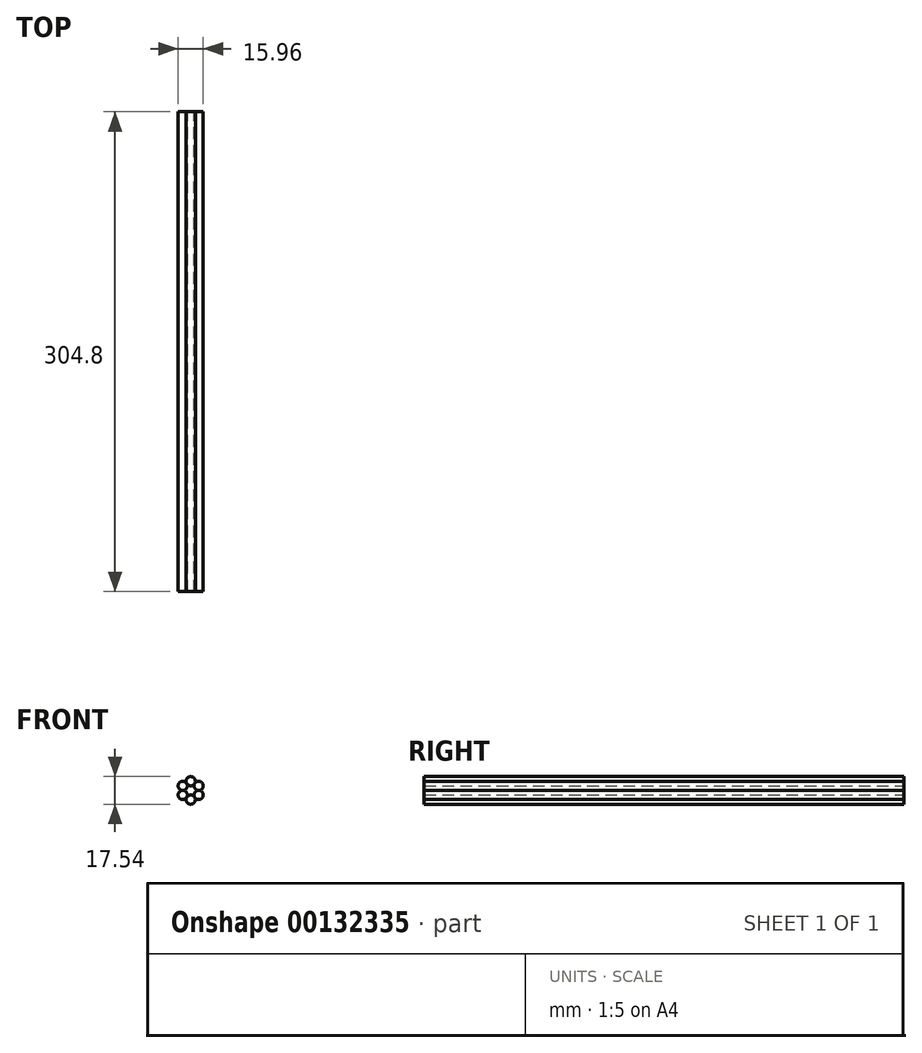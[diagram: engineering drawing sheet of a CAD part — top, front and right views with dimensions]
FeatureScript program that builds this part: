
annotation { "Feature Type Name" : "Feature", "Feature Type Description" : "" }
export const myFeature = defineFeature(function(context is Context, id is Id, definition is map)
    precondition{}
    {
        {
            var Q0;
            Q0=qCreatedBy(makeId("Front.planeOp"),FACE);
            var sketch = newSketch(context, id + "F0", { "sketchPlane" : qUnion([Q0])});
            skCircle(sketch, "E0", {"center": v(0, 0) * mm, "radius": 2.92 * mm});
            skCircle(sketch, "E1", {"center": v(-5.05, -2.93) * mm, "radius": 2.92 * mm});
            skCircle(sketch, "E2", {"center": v(-5.05, -8.77) * mm, "radius": 2.92 * mm});
            skCircle(sketch, "E3", {"center": v(0, -11.7) * mm, "radius": 2.92 * mm});
            skCircle(sketch, "E4", {"center": v(5.05, -8.77) * mm, "radius": 2.92 * mm});
            skCircle(sketch, "E5", {"center": v(5.05, -2.93) * mm, "radius": 2.92 * mm});
            skSolve(sketch);
        }
        {
            var Q0;
            {var subQ0=sQuery(id+"F0.wireOp",EDGE,"E0");var subQ1=makeQuery(id+"F0.imprint","INTERSECT",VERTEX,{"derivedFrom":[subQ0,sQuery(id+"F0.wireOp",EDGE,"E1")]});Q0=makeQuery(id+"F0.imprint","IMPRINT",FACE,{"disambiguationData":[TD([[makeQuery(id+"F0.imprint","IMPRINT",EDGE,{"disambiguationData":[TD([[subQ1,-1.0]])],"derivedFrom":subQ0}),1.0]])]});}
            var Q1;
            {var subQ0=sQuery(id+"F0.wireOp",EDGE,"E1");var subQ1=makeQuery(id+"F0.imprint","INTERSECT",VERTEX,{"derivedFrom":[sQuery(id+"F0.wireOp",EDGE,"E0"),subQ0]});Q1=makeQuery(id+"F0.imprint","IMPRINT",FACE,{"disambiguationData":[TD([[makeQuery(id+"F0.imprint","IMPRINT",EDGE,{"disambiguationData":[TD([[subQ1,-1.0]])],"derivedFrom":subQ0}),1.0]])]});}
            var Q2;
            {var subQ0=sQuery(id+"F0.wireOp",EDGE,"E2");var subQ1=makeQuery(id+"F0.imprint","INTERSECT",VERTEX,{"derivedFrom":[sQuery(id+"F0.wireOp",EDGE,"E1"),subQ0]});Q2=makeQuery(id+"F0.imprint","IMPRINT",FACE,{"disambiguationData":[TD([[makeQuery(id+"F0.imprint","IMPRINT",EDGE,{"disambiguationData":[TD([[subQ1,-1.0]])],"derivedFrom":subQ0}),1.0]])]});}
            var Q3;
            {var subQ0=sQuery(id+"F0.wireOp",EDGE,"E3");var subQ1=makeQuery(id+"F0.imprint","INTERSECT",VERTEX,{"derivedFrom":[sQuery(id+"F0.wireOp",EDGE,"E2"),subQ0]});Q3=makeQuery(id+"F0.imprint","IMPRINT",FACE,{"disambiguationData":[TD([[makeQuery(id+"F0.imprint","IMPRINT",EDGE,{"disambiguationData":[TD([[subQ1,1.0]])],"derivedFrom":subQ0}),1.0]])]});}
            var Q4;
            {var subQ0=sQuery(id+"F0.wireOp",EDGE,"E4");var subQ1=makeQuery(id+"F0.imprint","INTERSECT",VERTEX,{"derivedFrom":[sQuery(id+"F0.wireOp",EDGE,"E3"),subQ0]});Q4=makeQuery(id+"F0.imprint","IMPRINT",FACE,{"disambiguationData":[TD([[makeQuery(id+"F0.imprint","IMPRINT",EDGE,{"disambiguationData":[TD([[subQ1,1.0]])],"derivedFrom":subQ0}),1.0]])]});}
            var Q5;
            {var subQ0=sQuery(id+"F0.wireOp",EDGE,"E5");var subQ1=makeQuery(id+"F0.imprint","INTERSECT",VERTEX,{"derivedFrom":[sQuery(id+"F0.wireOp",EDGE,"E0"),subQ0]});Q5=makeQuery(id+"F0.imprint","IMPRINT",FACE,{"disambiguationData":[TD([[makeQuery(id+"F0.imprint","IMPRINT",EDGE,{"disambiguationData":[TD([[subQ1,-1.0]])],"derivedFrom":subQ0}),1.0]])]});}
            extrude(context, id + "F1", {"entities" : qUnion([Q0, Q1, Q2, Q3, Q4, Q5]), "depth" : 304.8 * mm});
        }
    });
